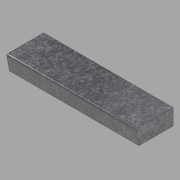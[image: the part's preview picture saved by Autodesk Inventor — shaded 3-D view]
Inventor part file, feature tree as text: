
AUTODESK INVENTOR PART (.ipt)
format: ipt  version: 2022.1 (Build 261234020, 234B)  size: 100,352 bytes
history: native  units: in
note: dims shown in document units (in); Inventor stores cm internally (conversion verified against a paired STEP export)
features: extrude x1, sketch x1
ambient origin geometry x8: Origin, YZ Plane, XZ Plane, XY Plane, X Axis, Y Axis, Z Axis, Center Point
bodies: Solid1 (feature_tree)
feature tree (2):
  extrude  "Extrusion1"  Depth=13.0in
  sketch  "Sketch1"  dims[d0=6.0in d1=13.0in d2=13.5in d3=0.5in d4=49.1953in d5=0.0in]
